# Revit family: TowelHolder-Long-Vitra-BaseSeries-A44131
name_source: partatom
category: Plumbing Fixtures
revit_build: Autodesk Revit 2017 (Build: 20160225_1515(x64)
units: mm (PartAtom-declared; Revit-internal decimal feet)

## family parameters
Cut with Voids When Loaded = No
Host = Face
OmniClass Number = 23.45.55.00
OmniClass Title = Sanitary Faucets, Wastes
Part Type = Normal
Room Calculation Point = No
Round Connector Dimension = Use Diameter
Shared = Yes

## types (2) — shared parameters
BIMobject category = Sanitary - Bathroom Accessories
Brand = VitrA
CW Connection = No
Default Elevation = 1050 mm
Description = Base Towel Holder - Long
Design country = Turkey
HW Connection = No
IFC Classification = Sanitary Terminal
Main Material = Metal
Manufacturer = Vitra
Manufacturer name = Vitra
Mounting type = Wall Mounted
NBS Referans Code = 35-75-90
NBS Referans Description = Towel Rails
Nominal Depth (mm) = 70 mm  [stored 0.229659 ft]
Nominal Height (mm) = 50 mm  [stored 0.164042 ft]
Nominal Width (mm) = 500 mm  [stored 1.64042 ft]
OmniClass Code = 23-31 25 25
OmniClass Description = Towel Bars
Product Type = Built In Towel Holder Long
Product certification = https://www.vitraglobal.com
Product family = Base Series
Product group = Towel Holder Long
Product url = https://vitraglobal.com
Technical description = https://vitraglobal.com
UNSPSC Description = Furniture and Furnishings
URL = https://vitraglobal.com
Uniclass 1.4 Code = L8245
Uniclass 1.4 Description = Towel rails
Uniclass 2.0 Code = PR-35-75-90
Uniclass 2.0 Description = Towel Rails
Uniclass 2015 Code = Pr_40_20_76_90
Uniclass 2015 Name = Towel rails
Uniformat II Code = E2010
Uniformat II Description = FURNISHINGS
Vent Connection = No
Warranty Period (Year) = 5 years
Waste Connection = No
Weight Net (kg) = 2
Youtube = https://www.youtube.com

## per-type parameters (varying)
| type | Article No. (default) | Coating Material | Color | Model | Product SKU |
| TowelHolder-Long-Vitra-BaseSeries-A44131 | A44131 | Chrome (Metal) | Chrome | A44131 | A44131 |
| TowelHolder-Long-Vitra-BaseSeries-A4413136 | A4413136 | Matte Black (Metal) | Matte Black | A4413136 | A4413136 |

note: [stored X ft] marks values corroborated as IEEE doubles in the binary element streams (Revit-internal decimal feet)

## geometry (parser evidence)
native form markers: Sweep x3
no freeform markers — native parametric forms only
